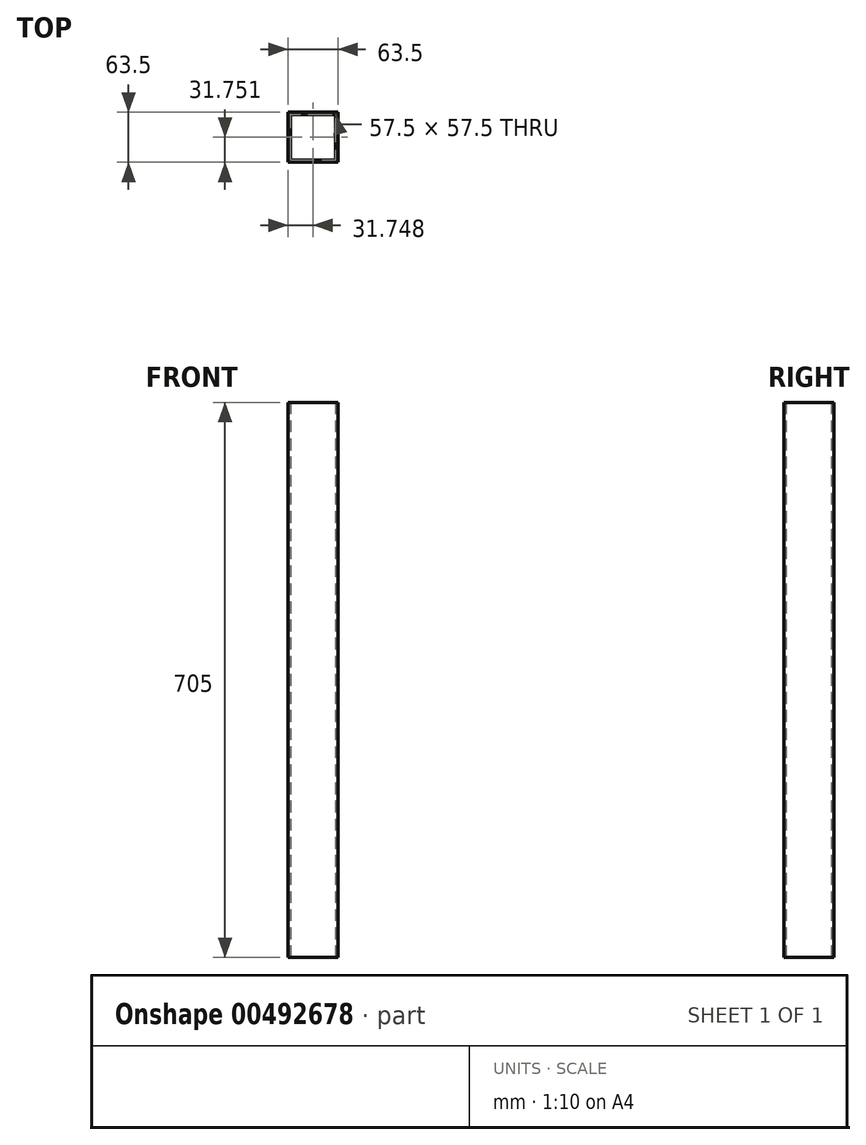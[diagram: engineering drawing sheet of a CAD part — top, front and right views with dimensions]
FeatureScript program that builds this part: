
annotation { "Feature Type Name" : "Feature", "Feature Type Description" : "" }
export const myFeature = defineFeature(function(context is Context, id is Id, definition is map)
    precondition{}
    {
        {
            var Q0;
            Q0=qCreatedBy(makeId("Top.planeOp"),FACE);
            var sketch = newSketch(context, id + "F0", { "sketchPlane" : qUnion([Q0])});
            skLineSegment(sketch, "E0.bottom", {"start": v(-22.96, 19.1) * mm, "end": v(34.54, 19.1) * mm});
            skLineSegment(sketch, "E0.top", {"start": v(-22.96, -38.4) * mm, "end": v(34.54, -38.4) * mm});
            skLineSegment(sketch, "E0.left", {"start": v(-22.96, 19.1) * mm, "end": v(-22.96, -38.4) * mm});
            skLineSegment(sketch, "E0.right", {"start": v(34.54, 19.1) * mm, "end": v(34.54, -38.4) * mm});
            skLineSegment(sketch, "E1.bottom", {"start": v(-25.96, 22.1) * mm, "end": v(37.54, 22.1) * mm});
            skLineSegment(sketch, "E1.top", {"start": v(-25.96, -41.4) * mm, "end": v(37.54, -41.4) * mm});
            skLineSegment(sketch, "E1.left", {"start": v(-25.96, 22.1) * mm, "end": v(-25.96, -41.4) * mm});
            skLineSegment(sketch, "E1.right", {"start": v(37.54, 22.1) * mm, "end": v(37.54, -41.4) * mm});
            skSolve(sketch);
        }
        {
            var Q0;
            Q0 = qSketchRegion(id + "F0", true);
            extrude(context, id + "F1", {"entities" : qUnion([Q0]), "flatOperationType" : FlatOperationType.REMOVE, "offsetDistance" : 25 * mm, "depth" : 705 * mm, "domain" : OperationDomain.MODEL});
        }
    });
